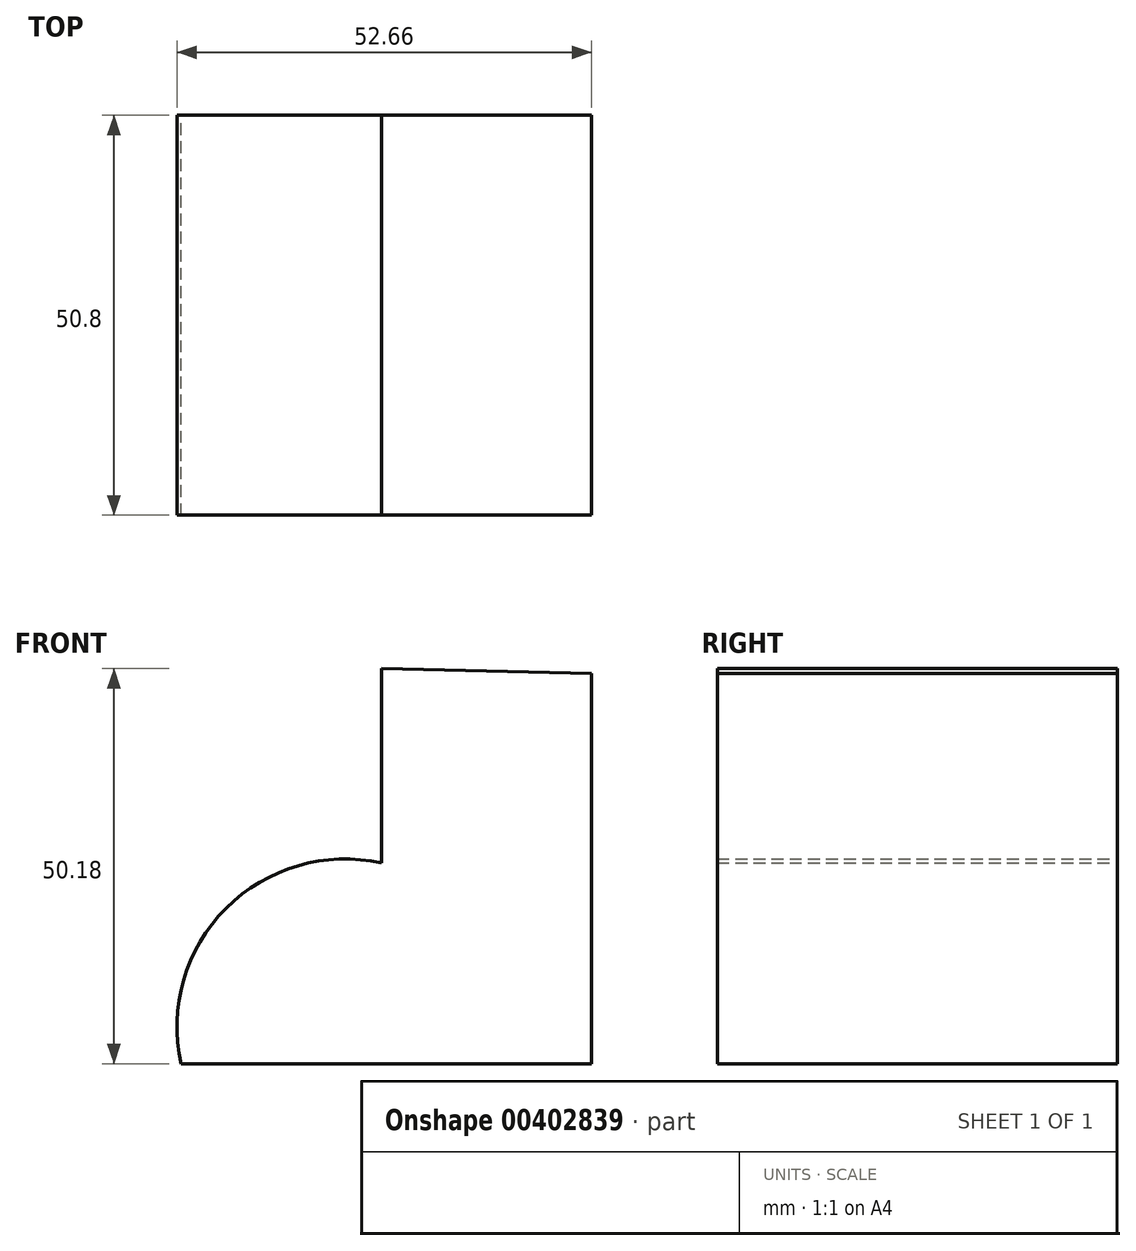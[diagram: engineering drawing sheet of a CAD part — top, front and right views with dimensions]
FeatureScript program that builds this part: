
annotation { "Feature Type Name" : "Feature", "Feature Type Description" : "" }
export const myFeature = defineFeature(function(context is Context, id is Id, definition is map)
    precondition{}
    {
        {
            var Q0;
            Q0=qCreatedBy(makeId("Front.planeOp"),FACE);
            var sketch = newSketch(context, id + "F0", { "sketchPlane" : qUnion([Q0])});
            skLineSegment(sketch, "E0", {"start": v(18.37, 30.23) * mm, "end": v(18.37, -19.36) * mm});
            skLineSegment(sketch, "E1", {"start": v(18.37, -19.36) * mm, "end": v(-33.78, -19.36) * mm});
            skLineSegment(sketch, "E2", {"start": v(-8.3, 6.12) * mm, "end": v(-8.3, 30.82) * mm});
            skLineSegment(sketch, "E3", {"start": v(18.37, 30.23) * mm, "end": v(-8.3, 30.82) * mm});
            skArc(sketch, "E4", {"start": v(-8.3, 6.12) * mm, "mid": v(-28.04, 0.38) * mm, "end": v(-33.78, -19.36) * mm});
            skSolve(sketch);
        }
        {
            var Q0;
            Q0 = qSketchRegion(id + "F0", true);
            extrude(context, id + "F1", {"entities" : qUnion([Q0]), "depth" : 50.8 * mm});
        }
    });
